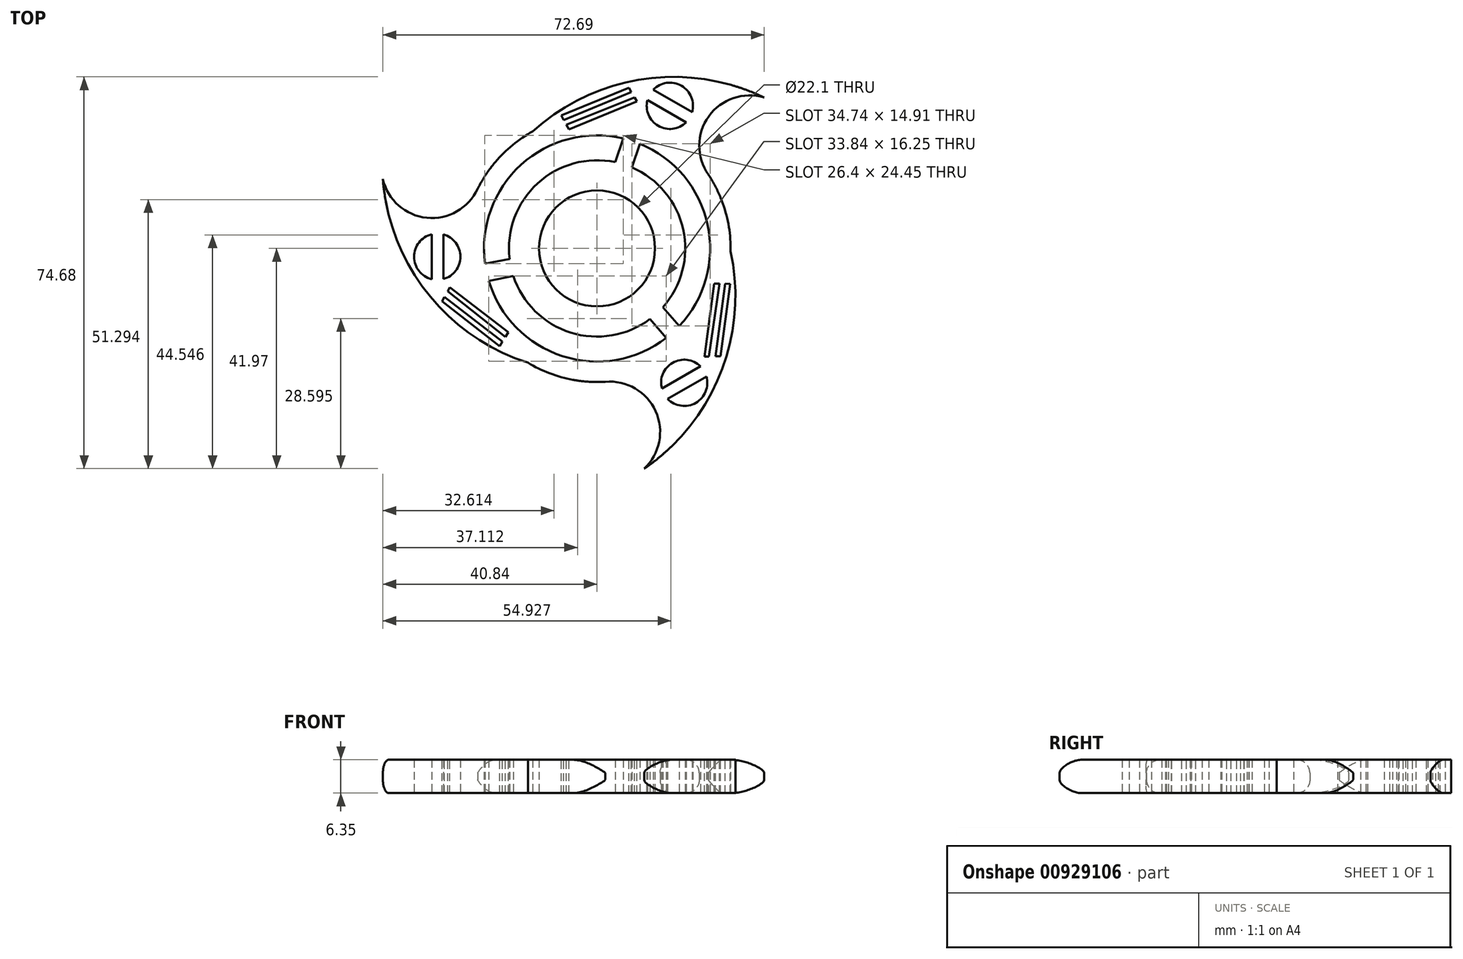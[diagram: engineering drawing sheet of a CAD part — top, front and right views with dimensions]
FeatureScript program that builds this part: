
annotation { "Feature Type Name" : "Feature", "Feature Type Description" : "" }
export const myFeature = defineFeature(function(context is Context, id is Id, definition is map)
    precondition{}
    {
        {
            var Q0;
            Q0=qCreatedBy(makeId("Top.planeOp"),FACE);
            var sketch = newSketch(context, id + "F0", { "sketchPlane" : qUnion([Q0])});
            skCircle(sketch, "E0", {"center": v(0, 0) * mm, "radius": 25.46 * mm});
            skArc(sketch, "E1", {"start": v(31.85, 28.77) * mm, "mid": v(8.81, 32.29) * mm, "end": v(-12.25, 22.32) * mm});
            skArc(sketch, "E2", {"start": v(31.85, 28.77) * mm, "mid": v(21.3, 25.2) * mm, "end": v(21.24, 14.04) * mm});
            skArc(sketch, "E3.1.0", {"start": v(-40.84, 13.2) * mm, "mid": v(-32.46, 5.84) * mm, "end": v(-22.78, 11.37) * mm});
            skArc(sketch, "E3.1.1", {"start": v(-40.84, 13.2) * mm, "mid": v(-32.37, -8.5) * mm, "end": v(-13.2, -21.77) * mm});
            skArc(sketch, "E3.2.0", {"start": v(8.99, -41.97) * mm, "mid": v(11.17, -31.04) * mm, "end": v(1.54, -25.41) * mm});
            skArc(sketch, "E3.2.1", {"start": v(8.99, -41.97) * mm, "mid": v(23.55, -23.78) * mm, "end": v(25.45, -0.55) * mm});
            skSolve(sketch);
        }
        {
            var Q0;
            {var subQ0=sQuery(id+"F0.wireOp",EDGE,"E0");var subQ7=makeQuery(id+"F0.imprint","INTERSECT",VERTEX,{"derivedFrom":[subQ0,sQuery(id+"F0.wireOp",EDGE,"E1")]});Q0=makeQuery(id+"F0.imprint","IMPRINT",FACE,{"disambiguationData":[TD([[makeQuery(id+"F0.imprint","IMPRINT",EDGE,{"disambiguationData":[TD([[subQ7,1.0]])],"derivedFrom":subQ0}),1.0]])]});}
            var Q1;
            {var subQ0=sQuery(id+"F0.wireOp",EDGE,"E3.1.1");Q1=makeQuery(id+"F0.imprint","IMPRINT",FACE,{"disambiguationData":[TD([[makeQuery(id+"F0.imprint","IMPRINT",EDGE,{"derivedFrom":subQ0}),1.0]])]});}
            var Q2;
            {var subQ0=sQuery(id+"F0.wireOp",EDGE,"E1");Q2=makeQuery(id+"F0.imprint","IMPRINT",FACE,{"disambiguationData":[TD([[makeQuery(id+"F0.imprint","IMPRINT",EDGE,{"derivedFrom":subQ0}),1.0]])]});}
            var Q3;
            {var subQ0=sQuery(id+"F0.wireOp",EDGE,"E3.2.1");Q3=makeQuery(id+"F0.imprint","IMPRINT",FACE,{"disambiguationData":[TD([[makeQuery(id+"F0.imprint","IMPRINT",EDGE,{"derivedFrom":subQ0}),1.0]])]});}
            extrude(context, id + "F1", {"entities" : qUnion([Q0, Q1, Q2, Q3]), "depth" : 6.35 * mm, "offsetDistance" : 25.4 * mm});
        }
        {
            var Q0;
            Q0=makeQuery(id+"F1.opExtrude","CAP_FACE",FACE,{"disambiguationData":[OSD([sQuery(id+"F0.wireOp",EDGE,"E0"),sQuery(id+"F0.wireOp",EDGE,"E1"),sQuery(id+"F0.wireOp",EDGE,"E2"),sQuery(id+"F0.wireOp",EDGE,"E3.1.0"),sQuery(id+"F0.wireOp",EDGE,"E3.1.1"),sQuery(id+"F0.wireOp",EDGE,"E3.2.0"),sQuery(id+"F0.wireOp",EDGE,"E3.2.1")])],"isStart":true});
            var sketch = newSketch(context, id + "F2", { "sketchPlane" : qUnion([Q0])});
            skCircle(sketch, "E4", {"center": v(0, 0) * mm, "radius": 11.05 * mm});
            skSolve(sketch);
        }
        {
            var Q0;
            Q0 = qSketchRegion(id + "F2", true);
            extrude(context, id + "F3", {"entities" : qUnion([Q0]), "operationType" : NewBodyOperationType.REMOVE, "oppositeDirection" : true, "depth" : 25.4 * mm, "offsetDistance" : 25.4 * mm});
        }
        {
            var Q0;
            Q0=makeQuery(id+"F1.opExtrude","CAP_FACE",FACE,{"disambiguationData":[OSD([sQuery(id+"F0.wireOp",EDGE,"E0"),sQuery(id+"F0.wireOp",EDGE,"E1"),sQuery(id+"F0.wireOp",EDGE,"E2"),sQuery(id+"F0.wireOp",EDGE,"E3.1.0"),sQuery(id+"F0.wireOp",EDGE,"E3.1.1"),sQuery(id+"F0.wireOp",EDGE,"E3.2.0"),sQuery(id+"F0.wireOp",EDGE,"E3.2.1")])],"isStart":true});
            var sketch = newSketch(context, id + "F4", { "sketchPlane" : qUnion([Q0])});
            skCircle(sketch, "E5", {"center": v(0, 0) * mm, "radius": 16.8 * mm});
            skCircle(sketch, "E6", {"center": v(0, 0) * mm, "radius": 21.55 * mm});
            skLineSegment(sketch, "E7", {"start": v(13.2, 17.04) * mm, "end": v(10.06, 13.46) * mm});
            skLineSegment(sketch, "E8", {"start": v(15.67, 14.8) * mm, "end": v(12.53, 11.2) * mm});
            skLineSegment(sketch, "E9.1.0", {"start": v(-21.36, 2.9) * mm, "end": v(-16.7, 1.98) * mm});
            skLineSegment(sketch, "E9.1.1", {"start": v(-20.65, 6.18) * mm, "end": v(-15.97, 5.25) * mm});
            skLineSegment(sketch, "E9.2.0", {"start": v(8.16, -19.95) * mm, "end": v(6.63, -15.44) * mm});
            skLineSegment(sketch, "E9.2.1", {"start": v(4.98, -20.97) * mm, "end": v(3.44, -16.45) * mm});
            skSolve(sketch);
        }
        {
            var Q0;
            {var subQ0=sQuery(id+"F4.wireOp",EDGE,"E7");Q0=makeQuery(id+"F4.imprint","IMPRINT",FACE,{"disambiguationData":[TD([[makeQuery(id+"F4.imprint","IMPRINT",EDGE,{"derivedFrom":subQ0}),-1.0]])]});}
            var Q1;
            {var subQ0=sQuery(id+"F4.wireOp",EDGE,"E8");Q1=makeQuery(id+"F4.imprint","IMPRINT",FACE,{"disambiguationData":[TD([[makeQuery(id+"F4.imprint","IMPRINT",EDGE,{"derivedFrom":subQ0}),1.0]])]});}
            var Q2;
            {var subQ0=sQuery(id+"F4.wireOp",EDGE,"E9.1.0");Q2=makeQuery(id+"F4.imprint","IMPRINT",FACE,{"disambiguationData":[TD([[makeQuery(id+"F4.imprint","IMPRINT",EDGE,{"derivedFrom":subQ0}),-1.0]])]});}
            extrude(context, id + "F5", {"entities" : qUnion([Q0, Q1, Q2]), "operationType" : NewBodyOperationType.REMOVE, "oppositeDirection" : true, "depth" : 25.4 * mm, "offsetDistance" : 25.4 * mm});
        }
        {
            var Q0;
            Q0=makeQuery(id+"F1.opExtrude","CAP_FACE",FACE,{"disambiguationData":[OSD([sQuery(id+"F0.wireOp",EDGE,"E0"),sQuery(id+"F0.wireOp",EDGE,"E1"),sQuery(id+"F0.wireOp",EDGE,"E2"),sQuery(id+"F0.wireOp",EDGE,"E3.1.0"),sQuery(id+"F0.wireOp",EDGE,"E3.1.1"),sQuery(id+"F0.wireOp",EDGE,"E3.2.0"),sQuery(id+"F0.wireOp",EDGE,"E3.2.1")])],"isStart":true});
            var sketch = newSketch(context, id + "F6", { "sketchPlane" : qUnion([Q0])});
            skCircle(sketch, "E10", {"center": v(-30.48, 1.58) * mm, "radius": 4.41 * mm});
            skCircle(sketch, "E11.1.0", {"center": v(13.87, -27.2) * mm, "radius": 4.41 * mm});
            skCircle(sketch, "E11.2.0", {"center": v(16.61, 25.6) * mm, "radius": 4.41 * mm});
            skPoint(sketch, "E11.center", {"position": v(0, 0) * mm});
            skLineSegment(sketch, "E12", {"start": v(-31.55, 5.86) * mm, "end": v(-31.55, -2.7) * mm});
            skLineSegment(sketch, "E13", {"start": v(-29.3, 5.83) * mm, "end": v(-29.3, -2.67) * mm});
            skLineSegment(sketch, "E14.1.0", {"start": v(10.7, -30.26) * mm, "end": v(18.11, -25.98) * mm});
            skLineSegment(sketch, "E14.1.1", {"start": v(9.6, -28.3) * mm, "end": v(16.96, -24.04) * mm});
            skLineSegment(sketch, "E14.2.0", {"start": v(20.85, 24.4) * mm, "end": v(13.44, 28.67) * mm});
            skLineSegment(sketch, "E14.2.1", {"start": v(19.7, 22.46) * mm, "end": v(12.34, 26.71) * mm});
            skSolve(sketch);
        }
        {
            var Q0;
            {var subQ0=sQuery(id+"F6.wireOp",EDGE,"E12");Q0=makeQuery(id+"F6.imprint","IMPRINT",FACE,{"disambiguationData":[TD([[makeQuery(id+"F6.imprint","IMPRINT",EDGE,{"derivedFrom":subQ0}),-1.0]])]});}
            var Q1;
            {var subQ0=sQuery(id+"F6.wireOp",EDGE,"E13");Q1=makeQuery(id+"F6.imprint","IMPRINT",FACE,{"disambiguationData":[TD([[makeQuery(id+"F6.imprint","IMPRINT",EDGE,{"derivedFrom":subQ0}),1.0]])]});}
            var Q2;
            {var subQ0=sQuery(id+"F6.wireOp",EDGE,"E14.2.0");Q2=makeQuery(id+"F6.imprint","IMPRINT",FACE,{"disambiguationData":[TD([[makeQuery(id+"F6.imprint","IMPRINT",EDGE,{"derivedFrom":subQ0}),-1.0]])]});}
            var Q3;
            {var subQ0=sQuery(id+"F6.wireOp",EDGE,"E14.2.1");Q3=makeQuery(id+"F6.imprint","IMPRINT",FACE,{"disambiguationData":[TD([[makeQuery(id+"F6.imprint","IMPRINT",EDGE,{"derivedFrom":subQ0}),1.0]])]});}
            var Q4;
            {var subQ0=sQuery(id+"F6.wireOp",EDGE,"E14.1.1");Q4=makeQuery(id+"F6.imprint","IMPRINT",FACE,{"disambiguationData":[TD([[makeQuery(id+"F6.imprint","IMPRINT",EDGE,{"derivedFrom":subQ0}),1.0]])]});}
            var Q5;
            {var subQ0=sQuery(id+"F6.wireOp",EDGE,"E14.1.0");Q5=makeQuery(id+"F6.imprint","IMPRINT",FACE,{"disambiguationData":[TD([[makeQuery(id+"F6.imprint","IMPRINT",EDGE,{"derivedFrom":subQ0}),-1.0]])]});}
            extrude(context, id + "F7", {"entities" : qUnion([Q0, Q1, Q2, Q3, Q4, Q5]), "operationType" : NewBodyOperationType.REMOVE, "oppositeDirection" : true, "depth" : 25.4 * mm, "offsetDistance" : 25.4 * mm});
        }
        {
            var Q0;
            Q0=makeQuery(id+"F1.opExtrude","CAP_EDGE",EDGE,{"disambiguationData":[OSD([sQuery(id+"F0.wireOp",EDGE,"E3.2.0")])],"isStart":false});
            var Q1;
            Q1=makeQuery(id+"F1.opExtrude","CAP_EDGE",EDGE,{"disambiguationData":[OSD([sQuery(id+"F0.wireOp",EDGE,"E3.1.0")])],"isStart":false});
            var Q2;
            Q2=makeQuery(id+"F1.opExtrude","CAP_EDGE",EDGE,{"disambiguationData":[OSD([sQuery(id+"F0.wireOp",EDGE,"E2")])],"isStart":false});
            var Q3;
            Q3=makeQuery(id+"F1.opExtrude","CAP_EDGE",EDGE,{"disambiguationData":[OSD([sQuery(id+"F0.wireOp",EDGE,"E3.1.0")])],"isStart":true});
            var Q4;
            Q4=makeQuery(id+"F1.opExtrude","CAP_EDGE",EDGE,{"disambiguationData":[OSD([sQuery(id+"F0.wireOp",EDGE,"E3.2.0")])],"isStart":true});
            var Q5;
            Q5=makeQuery(id+"F1.opExtrude","CAP_EDGE",EDGE,{"disambiguationData":[OSD([sQuery(id+"F0.wireOp",EDGE,"E2")])],"isStart":true});
            fillet(context, id + "F8", {"entities" : qUnion([Q0, Q1, Q2, Q3, Q4, Q5]), "radius" : 2.54 * mm, "tangentPropagation" : true, "allowEdgeOverflow" : false});
        }
        {
            var Q0;
            Q0=qCreatedBy(makeId("Top.planeOp"),FACE);
            var sketch = newSketch(context, id + "F9", { "sketchPlane" : qUnion([Q0])});
            skCircle(sketch, "E15", {"center": v(0, 0) * mm, "radius": 11.25 * mm});
            skSolve(sketch);
        }
        {
            var Q0;
            Q0=makeQuery(id+"F9.imprint","IMPRINT",FACE,{"disambiguationData":[TD([[makeQuery(id+"F9.imprint","IMPRINT",EDGE,{"derivedFrom":sQuery(id+"F9.wireOp",EDGE,"E15")}),1.0]])]});
            extrude(context, id + "F10", {"entities" : qUnion([Q0]), "operationType" : NewBodyOperationType.REMOVE, "oppositeDirection" : true, "depth" : 25.4 * mm, "offsetDistance" : 25.4 * mm});
        }
        {
            var Q0;
            Q0=makeQuery(id+"F1.opExtrude","CAP_FACE",FACE,{"disambiguationData":[OSD([sQuery(id+"F0.wireOp",EDGE,"E0"),sQuery(id+"F0.wireOp",EDGE,"E1"),sQuery(id+"F0.wireOp",EDGE,"E2"),sQuery(id+"F0.wireOp",EDGE,"E3.1.0"),sQuery(id+"F0.wireOp",EDGE,"E3.1.1"),sQuery(id+"F0.wireOp",EDGE,"E3.2.0"),sQuery(id+"F0.wireOp",EDGE,"E3.2.1")])],"isStart":false});
            var sketch = newSketch(context, id + "F11", { "sketchPlane" : qUnion([Q0])});
            skLineSegment(sketch, "E16", {"start": v(6.05, 30.64) * mm, "end": v(-6.84, 25.38) * mm});
            skLineSegment(sketch, "E17", {"start": v(6.54, 29.83) * mm, "end": v(-6.37, 24.5) * mm});
            skLineSegment(sketch, "E18", {"start": v(7.18, 28.77) * mm, "end": v(-5.86, 23.56) * mm});
            skLineSegment(sketch, "E19", {"start": v(7.62, 28.03) * mm, "end": v(-5.38, 22.67) * mm});
            skLineSegment(sketch, "E20", {"start": v(-5.38, 22.67) * mm, "end": v(-6.84, 25.38) * mm});
            skLineSegment(sketch, "E21", {"start": v(6.05, 30.64) * mm, "end": v(7.62, 28.03) * mm});
            skLineSegment(sketch, "E22.1.0", {"start": v(-29.56, -10.08) * mm, "end": v(-18.56, -18.61) * mm});
            skLineSegment(sketch, "E22.1.1", {"start": v(-29.1, -9.25) * mm, "end": v(-18.04, -17.77) * mm});
            skLineSegment(sketch, "E22.1.2", {"start": v(-28.5, -8.17) * mm, "end": v(-17.47, -16.85) * mm});
            skLineSegment(sketch, "E22.1.3", {"start": v(-28.08, -7.41) * mm, "end": v(-16.94, -16) * mm});
            skLineSegment(sketch, "E22.1.4", {"start": v(-29.56, -10.08) * mm, "end": v(-28.08, -7.41) * mm});
            skLineSegment(sketch, "E22.1.5", {"start": v(-16.94, -16) * mm, "end": v(-18.56, -18.61) * mm});
            skLineSegment(sketch, "E22.2.0", {"start": v(23.5, -20.55) * mm, "end": v(25.4, -6.76) * mm});
            skLineSegment(sketch, "E22.2.1", {"start": v(22.56, -20.57) * mm, "end": v(24.4, -6.73) * mm});
            skLineSegment(sketch, "E22.2.2", {"start": v(21.32, -20.6) * mm, "end": v(23.33, -6.7) * mm});
            skLineSegment(sketch, "E22.2.3", {"start": v(20.46, -20.61) * mm, "end": v(22.32, -6.67) * mm});
            skLineSegment(sketch, "E22.2.4", {"start": v(23.5, -20.55) * mm, "end": v(20.46, -20.61) * mm});
            skLineSegment(sketch, "E22.2.5", {"start": v(22.32, -6.67) * mm, "end": v(25.4, -6.76) * mm});
            skPoint(sketch, "E22.center", {"position": v(0, 0) * mm});
            skSolve(sketch);
        }
        {
            var Q0;
            {var subQ0=sQuery(id+"F11.wireOp",EDGE,"E16");Q0=makeQuery(id+"F11.imprint","IMPRINT",FACE,{"disambiguationData":[TD([[makeQuery(id+"F11.imprint","IMPRINT",EDGE,{"derivedFrom":subQ0}),1.0]])]});}
            var Q1;
            {var subQ0=sQuery(id+"F11.wireOp",EDGE,"E18");Q1=makeQuery(id+"F11.imprint","IMPRINT",FACE,{"disambiguationData":[TD([[makeQuery(id+"F11.imprint","IMPRINT",EDGE,{"derivedFrom":subQ0}),1.0]])]});}
            var Q2;
            {var subQ0=sQuery(id+"F11.wireOp",EDGE,"E22.2.0");Q2=makeQuery(id+"F11.imprint","IMPRINT",FACE,{"disambiguationData":[TD([[makeQuery(id+"F11.imprint","IMPRINT",EDGE,{"derivedFrom":subQ0}),1.0]])]});}
            var Q3;
            {var subQ0=sQuery(id+"F11.wireOp",EDGE,"E22.2.2");Q3=makeQuery(id+"F11.imprint","IMPRINT",FACE,{"disambiguationData":[TD([[makeQuery(id+"F11.imprint","IMPRINT",EDGE,{"derivedFrom":subQ0}),1.0]])]});}
            var Q4;
            {var subQ0=sQuery(id+"F11.wireOp",EDGE,"E22.1.0");Q4=makeQuery(id+"F11.imprint","IMPRINT",FACE,{"disambiguationData":[TD([[makeQuery(id+"F11.imprint","IMPRINT",EDGE,{"derivedFrom":subQ0}),1.0]])]});}
            var Q5;
            {var subQ0=sQuery(id+"F11.wireOp",EDGE,"E22.1.2");Q5=makeQuery(id+"F11.imprint","IMPRINT",FACE,{"disambiguationData":[TD([[makeQuery(id+"F11.imprint","IMPRINT",EDGE,{"derivedFrom":subQ0}),1.0]])]});}
            extrude(context, id + "F12", {"entities" : qUnion([Q0, Q1, Q2, Q3, Q4, Q5]), "operationType" : NewBodyOperationType.REMOVE, "oppositeDirection" : true, "depth" : 25.4 * mm, "offsetDistance" : 25.4 * mm});
        }
    });
